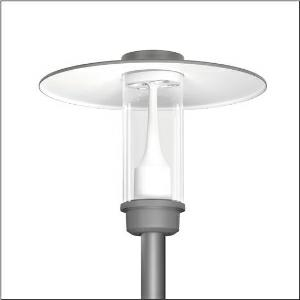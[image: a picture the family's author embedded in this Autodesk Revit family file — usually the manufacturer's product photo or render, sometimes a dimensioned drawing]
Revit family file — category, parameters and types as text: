
# Revit family: litepole_2_iq___st1_2a_5xa5425kf14hp_e686
name_source: partatom
category: Lighting Fixtures
units: mm (PartAtom-declared; Revit-internal decimal feet)

## family parameters
Cut with Voids When Loaded = No
Host = Face
Light Source = No
Part Type = Normal
Room Calculation Point = No
Round Connector Dimension = Use Diameter
Shared = No

## types (1)
- --- (1 x LED, 4980 lm, 33.6 W, 4000K)
    Apparent Load = 34 VA
    CIE Flux Codes = 22 59 92 98 100
    Color Rendering = 70
    Color Temperature = 4000K
    Default Elevation = 1800 mm
    Description = Litepole 2 iQ, mast luminaire, Module 540 iQ-SR, primary light control with 3 zone facetted reflector, of plastic, silver coated, highly specular, structured, primary optical cover: cover, of PMMA, transparent, light distribution: ST1.2a, light emission: direct distribution, primary light characteristic: asymmetric, installation type: post-top, LED, High Power LED, rated luminous flux: 4.980lm, luminous efficacy: 148lm/W, light colour: 740, colour temperature: 4000K, control gear: iQ Street-Remote, control: pre-setting: logarithmic dimming characteristic, Street-Remote, Auto-Match, Temp-Guard, Lumen-Switch, Night-Set, Smart-Wire, Light-Fading, Desk-Remote (wireless, voltage-free reading and setting of iQ features in the workshop via application-optimized NFC function/RFID function), optimised constant luminous flux control (CLO 2.0), with terminal, 6-pole, max. 2.5mm², mains connection: 230..240V, AC, 50/60Hz, start of lifetime: 34W, end of service life: 36W, reduction: 15W, luminaire housing, upper part, of aluminium, coated, Siteco® metallic grey (DB 702S), diameter: 750mm, height: 590mm, spigot size: d x l = 76 x 70mm (post-top) | with reducer (optional accessory) 60 x 70mm, mounting height: 3..5m, post-top mast mounting element, of diecast aluminium, coated, Siteco® metallic grey (DB 702S), Module 540 iQ-SR, traffic white (RAL 9016), equipment: Power, protection rating (complete): IP65, insulation class (complete): insulation class II (safety insulation), certification: CE, ENEC, VDE, packaging unit: 1 piece

Light Distribution: ST1.2a
    Height = 590 mm
    Lamp = 1 x LED
    Lamp Light Flux = 4980 lm
    Lamp Power = 33.6 W
    Lamp count = 1
    Length = 750 mm
    Luminous efficacy = 148 lm/W
    Manufacturer = Siteco
    ModVariant = No
    Model = 5XA5425KF14HP
    Number of Poles = 1
    OnlyDefault = Yes
    Power Factor = 1
    Product Name = Litepole 2 iQ | ST1.2a
    Product group = mast luminaire | pylon top
    ProductGroupID = 6100
    Protection Class = Protection class II
    Protection Degree = IP 65
    RLX_Detail_Level = 1
    RLX_Emergency_Light_Flux = 0 lm
    RLX_Emergency_Type = 0
    RLX_Emergency_Type_DB = No
    RlxData = <blob elided: 31873 chars, md5=4c0d05f7>
    Socket = socket
    Standby Power = 0 W
    System Light Flux = 4980 lm
    System Power = 34 W
    Type Comments = factory setting: luminous flux: 100 % | dim-lin: 254 | 695 mA
    Type Image = l_1006518.jpg
    URL = http://relux.com
    VarID = @adj_189685
    Voltage = 0 V
    Weight = 0.00 kg
    Width = 0 mm  [stored 0 ft]

note: [stored X ft] marks values corroborated as IEEE doubles in the binary element streams (Revit-internal decimal feet)

## geometry (parser evidence)
native form markers: Blend x4, Sweep x11
no freeform markers — native parametric forms only
